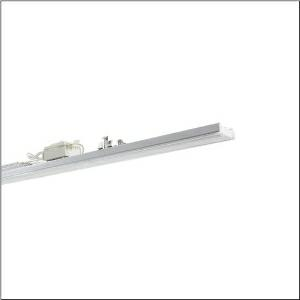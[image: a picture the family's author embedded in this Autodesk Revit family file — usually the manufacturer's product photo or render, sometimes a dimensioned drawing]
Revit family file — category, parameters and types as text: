
# Revit family: licross_r__11_recessed_mo_51te11cn49xg_6a24
name_source: partatom
category: Lighting Fixtures
units: mm (PartAtom-declared; Revit-internal decimal feet)

## family parameters
Cut with Voids When Loaded = No
Host = Face
Light Source = No
Part Type = Normal
Room Calculation Point = No
Round Connector Dimension = Use Diameter
Shared = No

## types (1)
- --- (1 x LED, 9160 lm, 49.3 W, 4000K)
    Apparent Load = 49 VA
    CIE Flux Codes = 89 96 99 100 100
    Color Rendering = 80
    Color Temperature = 4000K
    Default Elevation = 1800 mm
    Description = Licross® 11 Recessed MO, luminaire insert, of sheet steel, galvanised, coil coated, white, length: 1.500mm, width: 66mm, height: 67mm, LED rated luminous flux: 9.060lm, light colour: 840, control gear: ON/OFF Multilumen, CLOi, with plug, 3-pole, with phase selection, mains connection: 220..240V, AC, 50/60Hz, start of lifetime: 49W, end of service life: 55W, internal wiring halogen-free, primary light control with lens, of plastic, primary optical cover: cover, of PMMA, light emission: direct distribution, primary light characteristic: symmetric, protection rating (complete): IP54, insulation class (complete): insulation class I (protective earthing), certification: CE, ENEC, VDE, UKCA, protection symbol: D if used in an environment with non-conductive dust loads with corresponding accessories, impact resistance: IK06, permissible ambient temperature for indoor applications: -35..+40°C, corresponds to IFS (International Featured Standards) requirements for safety and quality in the food industry, reducing of maximum allowable ambient temperature of 5°C with ceiling mounting, LABS conformity tested according to VDMA 24364:2018-05, packaging unit: 1 piece
    Height = 58 mm
    Lamp = 1 x LED
    Lamp Light Flux = 9160 lm
    Lamp Power = 49.3 W
    Lamp count = 1
    Length = 1500 mm
    Luminous efficacy = 186 lm/W
    Manufacturer = Siteco
    ModVariant = No
    Model = 51TE11CN49XG
    Mounting Place = Ceiling
    Mounting Type = Pendant
    Number of Poles = 1
    OnlyDefault = Yes
    Power Factor = 1
    Product Name = Licross® 11 Recessed MO
    Product group = luminaire insert | ceiling pendant
    ProductGroupID = 902
    Protection Class = Protection class I
    Protection Degree = IP 54
    RLX_Detail_Level = 1
    RLX_Emergency_Light_Flux = 0 lm
    RLX_Emergency_Type = 0
    RLX_Emergency_Type_DB = No
    RlxData = <blob elided: 22289 chars, md5=00f5daa9>
    Socket = socket
    Standby Power = 0 W
    System Light Flux = 9160 lm
    System Power = 49 W
    Type Comments = factory setting: luminous flux: 100 % | (A | C | E) | 113 mA
    Type Image = l_1296930.jpg
    URL = http://relux.com
    VarID = @adj_105967
    Voltage = 0 V
    Weight = 0.00 kg
    Width = 66 mm

## geometry (parser evidence)
native form markers: Blend x4, Sweep x13
no freeform markers — native parametric forms only
